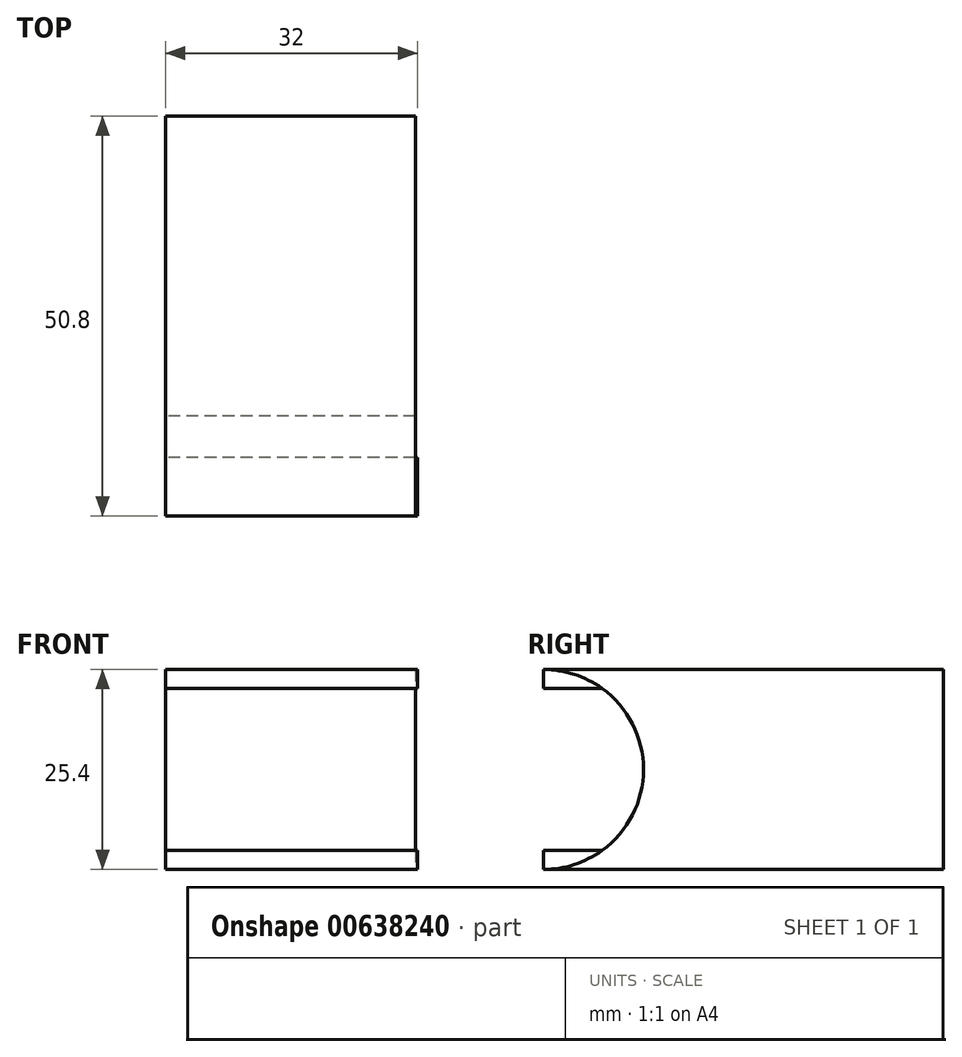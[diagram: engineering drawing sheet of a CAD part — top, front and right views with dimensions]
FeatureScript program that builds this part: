
annotation { "Feature Type Name" : "Feature", "Feature Type Description" : "" }
export const myFeature = defineFeature(function(context is Context, id is Id, definition is map)
    precondition{}
    {
        {
            var Q0;
            Q0=qCreatedBy(makeId("Front.planeOp"),FACE);
            var sketch = newSketch(context, id + "F0", { "sketchPlane" : qUnion([Q0])});
            skLineSegment(sketch, "E0.bottom", {"start": v(-13.34, -3.33) * mm, "end": v(18.4, -3.33) * mm});
            skLineSegment(sketch, "E0.top", {"start": v(-13.34, 22.07) * mm, "end": v(18.4, 22.07) * mm});
            skLineSegment(sketch, "E0.left", {"start": v(-13.34, -3.33) * mm, "end": v(-13.34, 22.07) * mm});
            skLineSegment(sketch, "E0.right", {"start": v(18.4, -3.33) * mm, "end": v(18.4, 22.07) * mm});
            skSolve(sketch);
        }
        {
            var Q0;
            Q0=makeQuery(id+"F0.imprint","IMPRINT",FACE,{"disambiguationData":[TD([[makeQuery(id+"F0.imprint","IMPRINT",EDGE,{"derivedFrom":sQuery(id+"F0.wireOp",EDGE,"E0.bottom")}),1.0]])]});
            extrude(context, id + "F1", {"entities" : qUnion([Q0]), "depth" : 50.8 * mm, "offsetDistance" : 25.4 * mm});
        }
        {
            var Q0;
            Q0=makeQuery(id+"F1.opExtrude","SWEPT_FACE",FACE,{"disambiguationData":[OSD([sQuery(id+"F0.wireOp",EDGE,"E0.left")])]});
            var sketch = newSketch(context, id + "F2", { "sketchPlane" : qUnion([Q0])});
            skLineSegment(sketch, "E1", {"start": v(50.8, 9.37) * mm, "end": v(38.1, 9.37) * mm});
            skArc(sketch, "E2", {"start": v(50.8, 22.07) * mm, "mid": v(41.82, 18.35) * mm, "end": v(38.1, 9.37) * mm});
            skArc(sketch, "E3", {"start": v(38.1, 9.37) * mm, "mid": v(41.82, 0.39) * mm, "end": v(50.8, -3.33) * mm});
            skSolve(sketch);
        }
        {
            var Q0;
            {var subQ0=sQuery(id+"F2.wireOp",EDGE,"E1");Q0=makeQuery(id+"F2.imprint","IMPRINT",FACE,{"disambiguationData":[TD([[makeQuery(id+"F2.imprint","IMPRINT",EDGE,{"derivedFrom":subQ0}),-1.0]])]});}
            var Q1;
            {var subQ0=sQuery(id+"F2.wireOp",EDGE,"E1");Q1=makeQuery(id+"F2.imprint","IMPRINT",FACE,{"disambiguationData":[TD([[makeQuery(id+"F2.imprint","IMPRINT",EDGE,{"derivedFrom":subQ0}),1.0]])]});}
            extrude(context, id + "F3", {"entities" : qUnion([Q0, Q1]), "operationType" : NewBodyOperationType.REMOVE, "oppositeDirection" : true, "depth" : 25.4 * mm, "offsetDistance" : 25.4 * mm});
        }
        {
            var Q0;
            Q0=makeQuery(id+"F3.boolean.opBoolean","COPY",FACE,{"derivedFrom":makeQuery(id+"F3.opExtrude","CAP_FACE",FACE,{"disambiguationData":[OSD([sQuery(id+"F0.wireOp",EDGE,"E0.left"),sQuery(id+"F2.wireOp",EDGE,"E2"),sQuery(id+"F2.wireOp",EDGE,"E3")])],"isStart":false})});
            extrude(context, id + "F4", {"entities" : qUnion([Q0]), "operationType" : NewBodyOperationType.REMOVE, "oppositeDirection" : true, "depth" : 25.4 * mm, "offsetDistance" : 25.4 * mm});
        }
        {
            var Q0;
            Q0=makeQuery(id+"F1.opExtrude","SWEPT_FACE",FACE,{"disambiguationData":[OSD([sQuery(id+"F0.wireOp",EDGE,"E0.left")])]});
            var sketch = newSketch(context, id + "F5", { "sketchPlane" : qUnion([Q0])});
            skLineSegment(sketch, "E4", {"start": v(50.8, 22.07) * mm, "end": v(50.8, 19.66) * mm});
            skLineSegment(sketch, "E5", {"start": v(50.8, 19.66) * mm, "end": v(43.36, 19.66) * mm});
            skLineSegment(sketch, "E6", {"start": v(50.8, -3.33) * mm, "end": v(50.8, -0.92) * mm});
            skLineSegment(sketch, "E7", {"start": v(50.8, -0.92) * mm, "end": v(43.35, -0.92) * mm});
            skSolve(sketch);
        }
        {
            var Q0;
            {var subQ0=sQuery(id+"F5.wireOp",EDGE,"E4");Q0=makeQuery(id+"F5.imprint","IMPRINT",FACE,{"disambiguationData":[TD([[makeQuery(id+"F5.imprint","IMPRINT",EDGE,{"derivedFrom":subQ0}),-1.0]])]});}
            var Q1;
            {var subQ0=sQuery(id+"F5.wireOp",EDGE,"E6");Q1=makeQuery(id+"F5.imprint","IMPRINT",FACE,{"disambiguationData":[TD([[makeQuery(id+"F5.imprint","IMPRINT",EDGE,{"derivedFrom":subQ0}),1.0]])]});}
            extrude(context, id + "F6", {"entities" : qUnion([Q0, Q1]), "oppositeDirection" : true, "depth" : 32 * mm, "offsetDistance" : 25.4 * mm});
        }
    });
